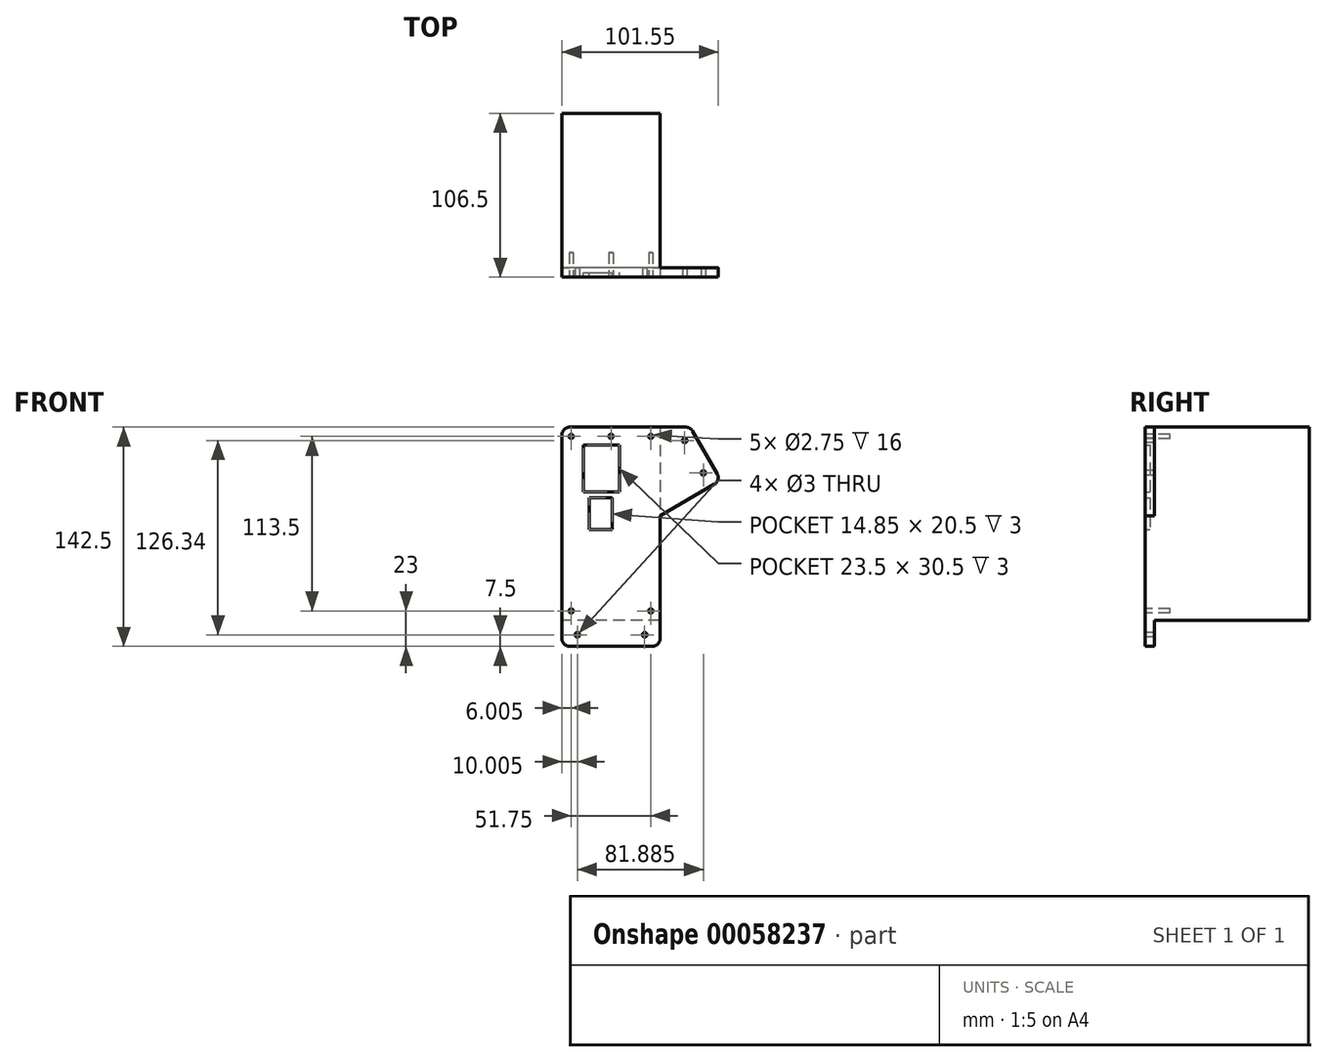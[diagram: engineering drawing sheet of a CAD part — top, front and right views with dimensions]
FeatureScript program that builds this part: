
annotation { "Feature Type Name" : "Feature", "Feature Type Description" : "" }
export const myFeature = defineFeature(function(context is Context, id is Id, definition is map)
    precondition{}
    {
        {
            var Q0;
            Q0=qCreatedBy(makeId("Front.planeOp"),FACE);
            var sketch = newSketch(context, id + "F0", { "sketchPlane" : qUnion([Q0])});
            skLineSegment(sketch, "E0.bottom", {"start": v(31.88, 62.75) * mm, "end": v(-31.88, 62.75) * mm});
            skLineSegment(sketch, "E0.top", {"start": v(31.88, -62.75) * mm, "end": v(-31.88, -62.75) * mm});
            skLineSegment(sketch, "E0.left", {"start": v(31.88, 62.75) * mm, "end": v(31.87, -62.75) * mm});
            skLineSegment(sketch, "E0.right", {"start": v(-31.87, 62.75) * mm, "end": v(-31.88, -62.75) * mm});
            skPoint(sketch, "E0.middle", {"position": v(0, 0) * mm});
            skSolve(sketch);
        }
        {
            var Q0;
            Q0 = qSketchRegion(id + "F0", true);
            extrude(context, id + "F1", {"entities" : qUnion([Q0]), "depth" : 100.5 * mm});
        }
        {
            var Q0;
            Q0=makeQuery(id+"F1.opExtrude","CAP_FACE",FACE,{"disambiguationData":[OSD([sQuery(id+"F0.wireOp",EDGE,"E0.bottom"),sQuery(id+"F0.wireOp",EDGE,"E0.top"),sQuery(id+"F0.wireOp",EDGE,"E0.left"),sQuery(id+"F0.wireOp",EDGE,"E0.right")])],"isStart":false});
            var sketch = newSketch(context, id + "F2", { "sketchPlane" : qUnion([Q0])});
            skLineSegment(sketch, "E1", {"start": v(-31.87, 56.75) * mm, "end": v(31.87, 56.75) * mm, "construction": true});
            skCircle(sketch, "E2", {"center": v(-25.88, 56.75) * mm, "radius": 1.38 * mm});
            skLineSegment(sketch, "E3", {"start": v(0, 56.75) * mm, "end": v(0, 0) * mm, "construction": true});
            skLineSegment(sketch, "E4", {"start": v(0, 0) * mm, "end": v(31.88, 0) * mm, "construction": true});
            skCircle(sketch, "E5", {"center": v(0, 56.75) * mm, "radius": 1.38 * mm});
            skCircle(sketch, "E6.MirrorC", {"center": v(25.87, 56.75) * mm, "radius": 1.38 * mm});
            skCircle(sketch, "E7.MirrorC", {"center": v(25.87, -56.75) * mm, "radius": 1.38 * mm});
            skCircle(sketch, "E8.MirrorC", {"center": v(-25.88, -56.75) * mm, "radius": 1.38 * mm});
            skSolve(sketch);
        }
        {
            var Q0;
            Q0 = qSketchRegion(id + "F2", true);
            extrude(context, id + "F3", {"entities" : qUnion([Q0]), "operationType" : NewBodyOperationType.REMOVE, "oppositeDirection" : true, "depth" : 10 * mm});
        }
        {
            var Q0;
            Q0=makeQuery(id+"F1.opExtrude","CAP_FACE",FACE,{"disambiguationData":[OSD([sQuery(id+"F0.wireOp",EDGE,"E0.bottom"),sQuery(id+"F0.wireOp",EDGE,"E0.top"),sQuery(id+"F0.wireOp",EDGE,"E0.left"),sQuery(id+"F0.wireOp",EDGE,"E0.right")])],"isStart":false});
            var sketch = newSketch(context, id + "F4", { "sketchPlane" : qUnion([Q0])});
            skLineSegment(sketch, "E9.bottom", {"start": v(-17.88, 51.25) * mm, "end": v(5.63, 51.25) * mm});
            skLineSegment(sketch, "E9.top", {"start": v(-17.88, 20.75) * mm, "end": v(5.63, 20.75) * mm});
            skLineSegment(sketch, "E9.left", {"start": v(-17.88, 51.25) * mm, "end": v(-17.88, 20.75) * mm});
            skLineSegment(sketch, "E9.right", {"start": v(5.63, 51.25) * mm, "end": v(5.63, 20.75) * mm});
            skLineSegment(sketch, "E10.bottom", {"start": v(-14.02, 16.75) * mm, "end": v(0.83, 16.75) * mm});
            skLineSegment(sketch, "E10.top", {"start": v(-14.02, -3.75) * mm, "end": v(0.83, -3.75) * mm});
            skLineSegment(sketch, "E10.left", {"start": v(-14.02, 16.75) * mm, "end": v(-14.02, -3.75) * mm});
            skLineSegment(sketch, "E10.right", {"start": v(0.83, 16.75) * mm, "end": v(0.83, -3.75) * mm});
            skSolve(sketch);
        }
        {
            var Q0;
            Q0 = qSketchRegion(id + "F4", true);
            extrude(context, id + "F5", {"entities" : qUnion([Q0]), "operationType" : NewBodyOperationType.ADD, "depth" : 3 * mm});
        }
        {
            var Q0;
            Q0=makeQuery(id+"F1.opExtrude","CAP_FACE",FACE,{"disambiguationData":[OSD([sQuery(id+"F0.wireOp",EDGE,"E0.bottom"),sQuery(id+"F0.wireOp",EDGE,"E0.top"),sQuery(id+"F0.wireOp",EDGE,"E0.left"),sQuery(id+"F0.wireOp",EDGE,"E0.right")])],"isStart":false});
            extrude(context, id + "F6", {"entities" : qUnion([Q0]), "depth" : 6 * mm});
        }
        {
            var Q0;
            Q0=makeQuery(id+"F6.opExtrude","CAP_FACE",FACE,{"disambiguationData":[OSD([sQuery(id+"F0.wireOp",EDGE,"E0.bottom"),sQuery(id+"F0.wireOp",EDGE,"E0.top"),sQuery(id+"F0.wireOp",EDGE,"E0.left"),sQuery(id+"F0.wireOp",EDGE,"E0.right")])],"isStart":false});
            var sketch = newSketch(context, id + "F7", { "sketchPlane" : qUnion([Q0])});
            skLineSegment(sketch, "E11", {"start": v(-66.71, 252.5) * mm, "end": v(120.79, -72.25) * mm, "construction": true});
            skLineSegment(sketch, "E12", {"start": v(120.79, -72.25) * mm, "end": v(-254.21, -72.25) * mm, "construction": true});
            skLineSegment(sketch, "E13", {"start": v(-254.21, -72.25) * mm, "end": v(-66.71, 252.5) * mm, "construction": true});
            skPoint(sketch, "E14", {"position": v(50.79, -72.25) * mm});
            skPoint(sketch, "E15", {"position": v(85.79, -11.63) * mm});
            skLineSegment(sketch, "E16", {"start": v(85.79, -11.63) * mm, "end": v(79.3, -15.38) * mm, "construction": true});
            skLineSegment(sketch, "E17", {"start": v(79.3, -15.38) * mm, "end": v(-71.04, 245) * mm, "construction": true});
            skLineSegment(sketch, "E18", {"start": v(50.79, -72.25) * mm, "end": v(50.79, -64.75) * mm, "construction": true});
            skLineSegment(sketch, "E19", {"start": v(50.79, -64.75) * mm, "end": v(-249.88, -64.75) * mm, "construction": true});
            skLineSegment(sketch, "E20", {"start": v(-71.04, 245) * mm, "end": v(-66.71, -64.75) * mm, "construction": true});
            skLineSegment(sketch, "E21.bottom", {"start": v(-31.88, -62.75) * mm, "end": v(31.87, -62.75) * mm});
            skLineSegment(sketch, "E21.top", {"start": v(-31.88, -79.75) * mm, "end": v(31.87, -79.75) * mm});
            skLineSegment(sketch, "E21.left", {"start": v(-31.87, -62.75) * mm, "end": v(-31.87, -79.75) * mm});
            skLineSegment(sketch, "E21.right", {"start": v(31.88, -62.75) * mm, "end": v(31.88, -79.75) * mm});
            skCircle(sketch, "E22", {"center": v(-21.88, -72.25) * mm, "radius": 1.5 * mm});
            skCircle(sketch, "E23", {"center": v(21.88, -72.25) * mm, "radius": 1.5 * mm});
            skLineSegment(sketch, "E24", {"start": v(31.88, 62.75) * mm, "end": v(31.87, 5.23) * mm});
            skLineSegment(sketch, "E25", {"start": v(31.88, 5.23) * mm, "end": v(71.5, 28.1) * mm});
            skLineSegment(sketch, "E26", {"start": v(71.5, 28.1) * mm, "end": v(51.5, 62.75) * mm});
            skLineSegment(sketch, "E27", {"start": v(51.5, 62.75) * mm, "end": v(31.88, 62.75) * mm});
            skCircle(sketch, "E28", {"center": v(47.84, 54.09) * mm, "radius": 1.5 * mm});
            skCircle(sketch, "E29", {"center": v(60, 33.02) * mm, "radius": 1.5 * mm});
            skLineSegment(sketch, "E30", {"start": v(61.5, 45.43) * mm, "end": v(55, 41.68) * mm, "construction": true});
            skPoint(sketch, "E31", {"position": v(42.84, 62.75) * mm});
            skSolve(sketch);
        }
        {
            var Q0;
            Q0 = qSketchRegion(id + "F7", true);
            var Q1;
            Q1=makeQuery(id+"F6.opExtrude","CAP_FACE",FACE,{"disambiguationData":[OSD([sQuery(id+"F0.wireOp",EDGE,"E0.bottom"),sQuery(id+"F0.wireOp",EDGE,"E0.top"),sQuery(id+"F0.wireOp",EDGE,"E0.left"),sQuery(id+"F0.wireOp",EDGE,"E0.right")])],"isStart":true});
            extrude(context, id + "F8", {"entities" : qUnion([Q0]), "operationType" : NewBodyOperationType.ADD, "endBound" : BoundingType.UP_TO_SURFACE, "oppositeDirection" : true, "endBoundEntityFace" : qUnion([Q1]), "depth" : 25 * mm});
        }
        {
            var Q0;
            Q0=makeQuery(id+"F6.opExtrude","SWEPT_EDGE",EDGE,{"disambiguationData":[OSD([sQuery(id+"F0.wireOp",EDGE,"E0.bottom"),sQuery(id+"F0.wireOp",EDGE,"E0.right")])]});
            var Q1;
            Q1=makeQuery(id+"F8.opExtrude","SWEPT_EDGE",EDGE,{"disambiguationData":[OSD([sQuery(id+"F7.wireOp",EDGE,"E21.top"),sQuery(id+"F7.wireOp",EDGE,"E21.right")])]});
            var Q2;
            Q2=makeQuery(id+"F8.opExtrude","SWEPT_EDGE",EDGE,{"disambiguationData":[OSD([sQuery(id+"F7.wireOp",EDGE,"E21.top"),sQuery(id+"F7.wireOp",EDGE,"E21.left")])]});
            var Q3;
            Q3=makeQuery(id+"F8.opExtrude","SWEPT_EDGE",EDGE,{"disambiguationData":[OSD([sQuery(id+"F7.wireOp",EDGE,"E25"),sQuery(id+"F7.wireOp",EDGE,"E26")])]});
            var Q4;
            Q4=makeQuery(id+"F8.opExtrude","SWEPT_EDGE",EDGE,{"disambiguationData":[OSD([sQuery(id+"F0.wireOp",EDGE,"E0.left"),sQuery(id+"F7.wireOp",EDGE,"E24"),sQuery(id+"F7.wireOp",EDGE,"E25")])]});
            var Q5;
            Q5=makeQuery(id+"F8.opExtrude","SWEPT_EDGE",EDGE,{"disambiguationData":[OSD([sQuery(id+"F7.wireOp",EDGE,"E26"),sQuery(id+"F7.wireOp",EDGE,"E27")])]});
            fillet(context, id + "F9", {"entities" : qUnion([Q0, Q1, Q2, Q3, Q4, Q5]), "radius" : 5 * mm, "tangentPropagation" : true, "allowEdgeOverflow" : false});
        }
    });
